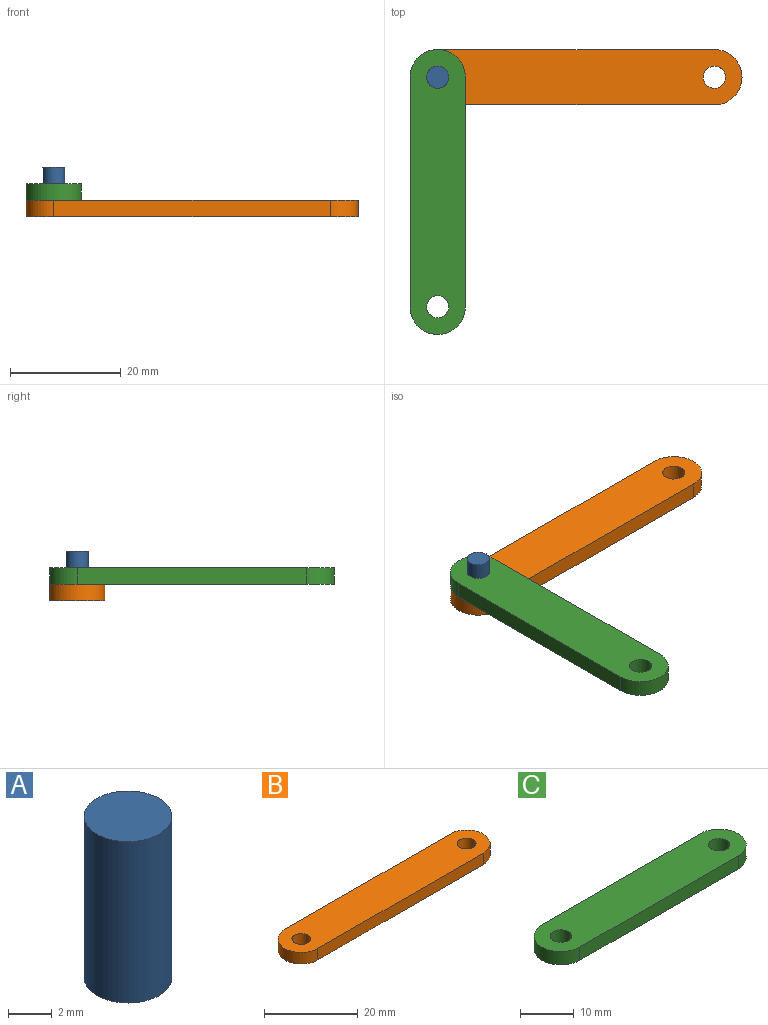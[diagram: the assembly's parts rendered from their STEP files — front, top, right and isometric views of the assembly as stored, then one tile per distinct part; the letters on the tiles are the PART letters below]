
ASSEMBLY  parts=3 mates=2
PART A: 3 faces, bbox 4x4x9 mm
  f0: cylinder r=2mm len=9mm, axis (0,0,-1), area 113.1mm2, adj f1,f2
  f1: plane 4x4mm, normal (0,0,1), area 12.6mm2, adj f0
  f2: plane 4x4mm, normal (0,0,-1), area 12.6mm2, adj f0
PART B: 8 faces, bbox 60x10x3 mm
  f0: plane 50x3mm, normal (0,-1,0), area 150mm2, adj f1,f5,f6,f7
  f1: cylinder r=5mm len=10mm, axis (0,0,-1), area 47.1mm2, adj f0,f2,f6,f7
  f2: plane 50x3mm, normal (0,1,0), area 150mm2, adj f1,f5,f6,f7
  f3: cylinder r=2mm len=4mm, axis (0,0,-1), area 37.7mm2, adj f6,f7
  f4: cylinder r=2mm len=4mm, axis (0,0,-1), area 37.7mm2, adj f6,f7
  f5: cylinder r=5mm len=10mm, axis (0,0,-1), area 47.1mm2, adj f0,f2,f6,f7
  f6: plane 60x10mm, normal (0,0,1), area 553.4mm2, adj f0,f1,f2,f3,f4,f5
  f7: plane 60x10mm, normal (0,0,-1), area 553.4mm2, adj f0,f1,f2,f3,f4,f5
PART C: 8 faces, bbox 51.5x10x3 mm
  f0: plane 41.5x3mm, normal (0,-1,0), area 124.5mm2, adj f1,f5,f6,f7
  f1: cylinder r=5mm len=10mm, axis (0,0,-1), area 47.1mm2, adj f0,f2,f6,f7
  f2: plane 41.5x3mm, normal (0,1,0), area 124.5mm2, adj f1,f5,f6,f7
  f3: cylinder r=2mm len=4mm, axis (0,0,-1), area 37.7mm2, adj f6,f7
  f4: cylinder r=2mm len=4mm, axis (0,0,-1), area 37.7mm2, adj f6,f7
  f5: cylinder r=5mm len=10mm, axis (0,0,-1), area 47.1mm2, adj f0,f2,f6,f7
  f6: plane 51.5x10mm, normal (0,0,1), area 468.4mm2, adj f0,f1,f2,f3,f4,f5
  f7: plane 51.5x10mm, normal (0,0,-1), area 468.4mm2, adj f0,f1,f2,f3,f4,f5
PLACE A t=(100.96,45.04,-4.5)mm
PLACE B t=(125.96,45.04,-4.5)mm
PLACE C rot(axis=(0,0,-1),90deg) t=(100.96,24.29,-1.5)mm
MATE fastened A.f0 <-> B.f3  axis (0,0,-1) through (100.96,45.04,-4.5)mm
MATE revolute A.f0 <-> C.f3  axis (0,0,-1) through (100.96,45.04,0)mm
